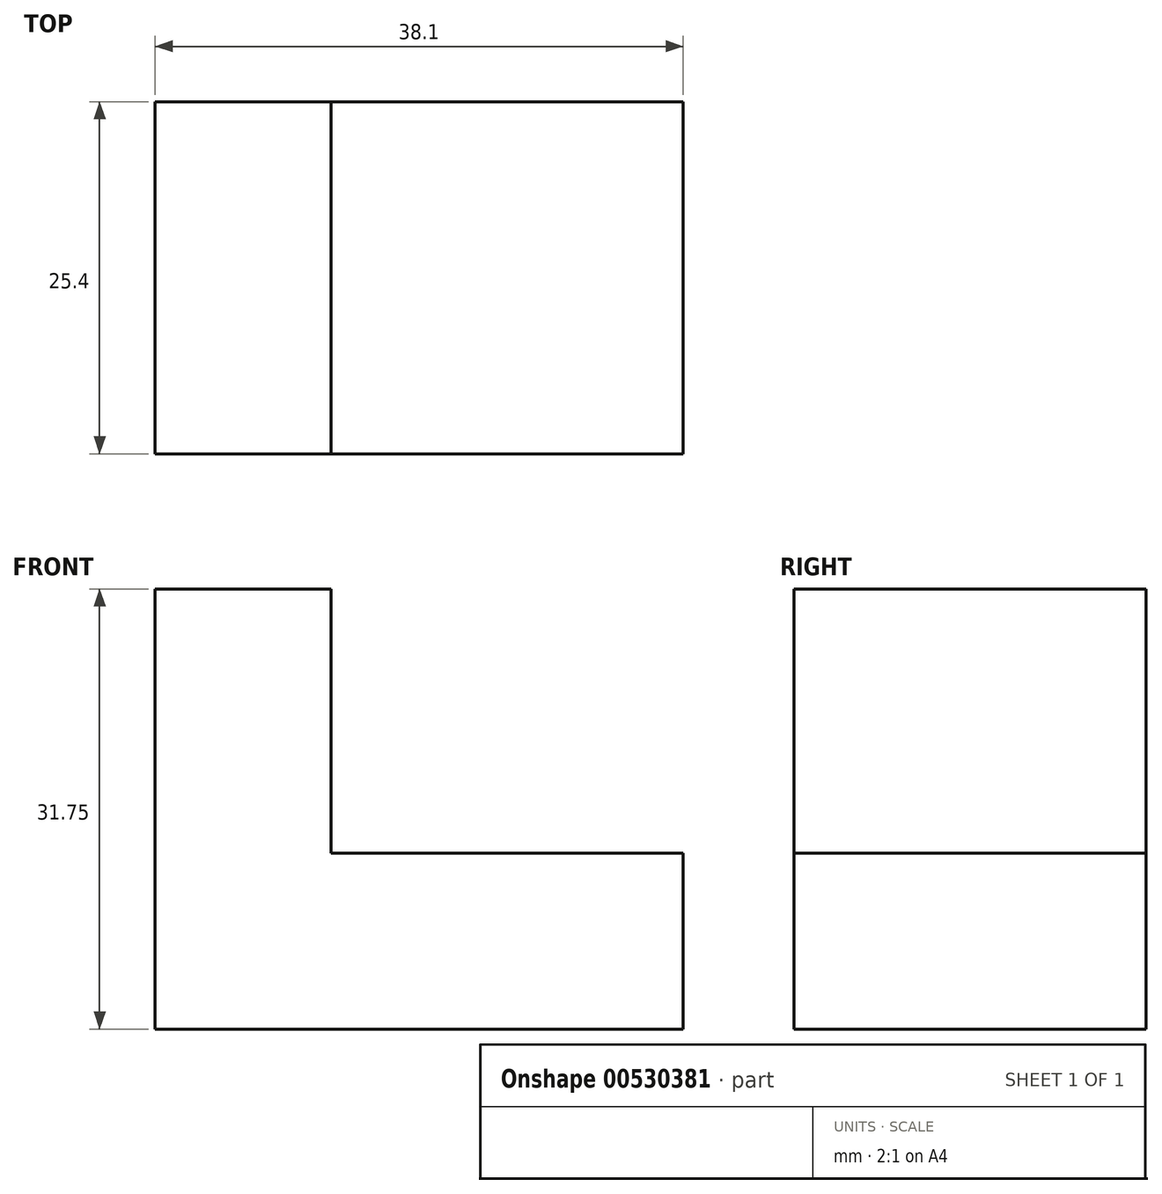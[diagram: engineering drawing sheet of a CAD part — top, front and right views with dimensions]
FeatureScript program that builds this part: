
annotation { "Feature Type Name" : "Feature", "Feature Type Description" : "" }
export const myFeature = defineFeature(function(context is Context, id is Id, definition is map)
    precondition{}
    {
        {
            var Q0;
            Q0=qCreatedBy(makeId("Front.planeOp"),FACE);
            var sketch = newSketch(context, id + "F0", { "sketchPlane" : qUnion([Q0])});
            skLineSegment(sketch, "E0", {"start": v(-38.1, 31.75) * mm, "end": v(-38.1, 0) * mm});
            skLineSegment(sketch, "E1", {"start": v(-38.1, 0) * mm, "end": v(0, 0) * mm});
            skLineSegment(sketch, "E2", {"start": v(0, 0) * mm, "end": v(0, 12.7) * mm});
            skLineSegment(sketch, "E3", {"start": v(0, 12.7) * mm, "end": v(-25.4, 12.7) * mm});
            skLineSegment(sketch, "E4", {"start": v(-25.4, 12.7) * mm, "end": v(-25.4, 31.75) * mm});
            skLineSegment(sketch, "E5", {"start": v(-25.4, 31.75) * mm, "end": v(-38.1, 31.75) * mm});
            skSolve(sketch);
        }
        {
            var Q0;
            Q0=makeQuery(id+"F0.imprint","IMPRINT",FACE,{"disambiguationData":[TD([[makeQuery(id+"F0.imprint","IMPRINT",EDGE,{"derivedFrom":sQuery(id+"F0.wireOp",EDGE,"E0")}),1.0]])]});
            extrude(context, id + "F1", {"entities" : qUnion([Q0]), "depth" : 25.4 * mm, "offsetDistance" : 25.4 * mm});
        }
    });
